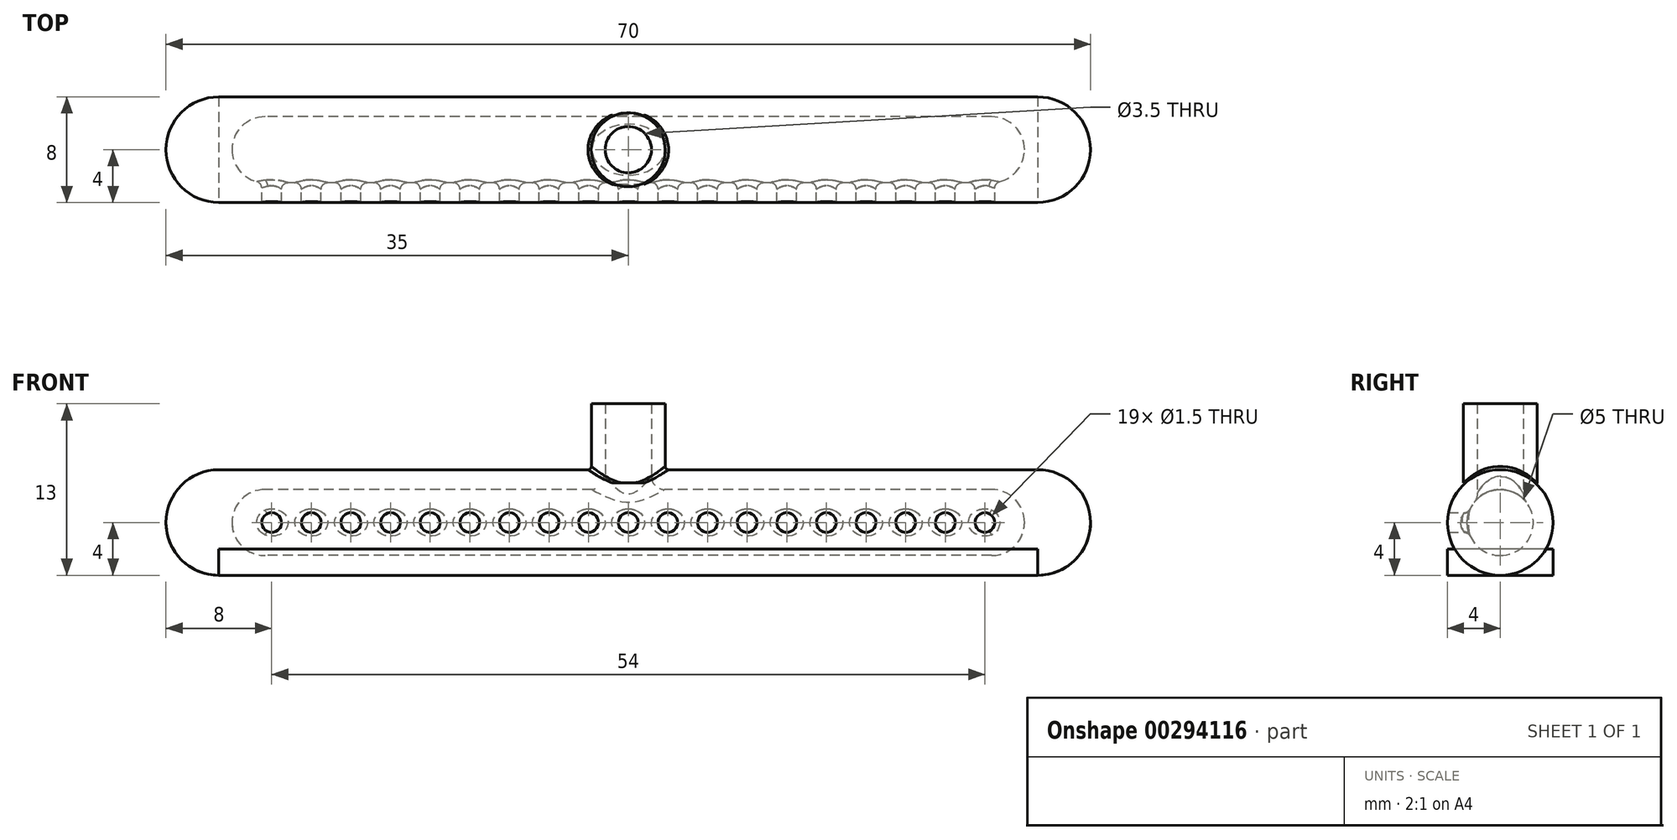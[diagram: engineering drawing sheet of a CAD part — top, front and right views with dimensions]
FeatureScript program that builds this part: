
annotation { "Feature Type Name" : "Feature", "Feature Type Description" : "" }
export const myFeature = defineFeature(function(context is Context, id is Id, definition is map)
    precondition{}
    {
        {
            var Q0;
            Q0=qCreatedBy(makeId("Top.planeOp"),FACE);
            var sketch = newSketch(context, id + "F0", { "sketchPlane" : qUnion([Q0])});
            skCircle(sketch, "E0", {"center": v(0, 0) * mm, "radius": 2.8 * mm});
            skCircle(sketch, "E1", {"center": v(0, 0) * mm, "radius": 1.75 * mm});
            skSolve(sketch);
        }
        {
            var Q0;
            Q0=makeQuery(id+"F0.imprint","IMPRINT",FACE,{"disambiguationData":[TD([[makeQuery(id+"F0.imprint","IMPRINT",EDGE,{"derivedFrom":sQuery(id+"F0.wireOp",EDGE,"E0")}),1.0]])]});
            extrude(context, id + "F1", {"entities" : qUnion([Q0]), "depth" : 6 * mm});
        }
        {
            var Q0;
            Q0=qCreatedBy(makeId("Right.planeOp"),FACE);
            var sketch = newSketch(context, id + "F2", { "sketchPlane" : qUnion([Q0])});
            skCircle(sketch, "E2", {"center": v(0, 0) * mm, "radius": 2.5 * mm});
            skSolve(sketch);
        }
        {
            var Q0;
            Q0 = qSketchRegion(id + "F2", true);
            extrude(context, id + "F3", {"entities" : qUnion([Q0]), "endBound" : BoundingType.SYMMETRIC, "depth" : 60 * mm});
        }
        {
            var Q0;
            Q0=makeQuery(id+"F3.opExtrude","SWEPT_BODY",BODY,{"disambiguationData":[OSD([sQuery(id+"F2.wireOp",EDGE,"E2")])]});
            transform(context, id + "F4", {"entities" : qUnion([Q0]), "transformType" : TransformType.TRANSLATION_3D, "dx" : 0 * mm, "dy" : 0 * mm, "dz" : -3 * mm, "makeCopy" : false});
        }
        {
            var Q0;
            Q0=makeQuery(id+"F3.opExtrude","CAP_EDGE",EDGE,{"disambiguationData":[OSD([sQuery(id+"F2.wireOp",EDGE,"E2")])],"isStart":false});
            var Q1;
            Q1=makeQuery(id+"F3.opExtrude","CAP_EDGE",EDGE,{"disambiguationData":[OSD([sQuery(id+"F2.wireOp",EDGE,"E2")])],"isStart":true});
            fillet(context, id + "F5", {"entities" : qUnion([Q0, Q1]), "radius" : 2.5 * mm, "tangentPropagation" : true, "allowEdgeOverflow" : false});
        }
        {
            var Q0;
            Q0=qCreatedBy(makeId("Top.planeOp"),FACE);
            var sketch = newSketch(context, id + "F6", { "sketchPlane" : qUnion([Q0])});
            skCircle(sketch, "E3", {"center": v(0, 0) * mm, "radius": 1.75 * mm});
            skSolve(sketch);
        }
        {
            var Q0;
            Q0 = qSketchRegion(id + "F6", true);
            extrude(context, id + "F7", {"entities" : qUnion([Q0]), "endBound" : BoundingType.SYMMETRIC, "depth" : 6 * mm});
        }
        {
            var Q0;
            Q0=makeQuery(id+"F7.opExtrude","SWEPT_BODY",BODY,{"disambiguationData":[OSD([sQuery(id+"F6.wireOp",EDGE,"E3")])]});
            var Q1;
            Q1=makeQuery(id+"F3.opExtrude","SWEPT_BODY",BODY,{"disambiguationData":[OSD([sQuery(id+"F2.wireOp",EDGE,"E2")])]});
            booleanBodies(context, id + "F8", {"operationType" : BooleanOperationType.UNION, "tools" : qUnion([Q0, Q1])});
        }
        {
            var Q0;
            Q0=qCreatedBy(makeId("Front.planeOp"),FACE);
            var sketch = newSketch(context, id + "F9", { "sketchPlane" : qUnion([Q0])});
            skCircle(sketch, "E4", {"center": v(-27, -3) * mm, "radius": 0.75 * mm});
            skCircle(sketch, "E5", {"center": v(-24, -3) * mm, "radius": 0.75 * mm});
            skCircle(sketch, "E6", {"center": v(-21, -3) * mm, "radius": 0.75 * mm});
            skCircle(sketch, "E7", {"center": v(-18, -3) * mm, "radius": 0.75 * mm});
            skCircle(sketch, "E8", {"center": v(-15, -3) * mm, "radius": 0.75 * mm});
            skCircle(sketch, "E9", {"center": v(-12, -3) * mm, "radius": 0.75 * mm});
            skCircle(sketch, "E10", {"center": v(-9, -3) * mm, "radius": 0.75 * mm});
            skCircle(sketch, "E11", {"center": v(-6, -3) * mm, "radius": 0.75 * mm});
            skCircle(sketch, "E12", {"center": v(-3, -3) * mm, "radius": 0.75 * mm});
            skCircle(sketch, "E13", {"center": v(0, -3) * mm, "radius": 0.75 * mm});
            skLineSegment(sketch, "E14.trimOffspring", {"start": v(-26.25, -3) * mm, "end": v(-27, -3) * mm});
            skLineSegment(sketch, "E15.trimOffspring", {"start": v(-23.25, -3) * mm, "end": v(-24, -3) * mm});
            skSolve(sketch);
        }
        {
            var Q0;
            Q0 = qSketchRegion(id + "F9", true);
            extrude(context, id + "F10", {"entities" : qUnion([Q0]), "depth" : 10 * mm});
        }
        {
            var Q0;
            Q0=makeQuery(id+"F10.opExtrude","SWEPT_BODY",BODY,{"disambiguationData":[OSD([sQuery(id+"F9.wireOp",EDGE,"E13")])]});
            var Q1;
            Q1=makeQuery(id+"F10.opExtrude","SWEPT_BODY",BODY,{"disambiguationData":[OSD([sQuery(id+"F9.wireOp",EDGE,"E12")])]});
            var Q2;
            Q2=makeQuery(id+"F10.opExtrude","SWEPT_BODY",BODY,{"disambiguationData":[OSD([sQuery(id+"F9.wireOp",EDGE,"E11")])]});
            var Q3;
            Q3=makeQuery(id+"F10.opExtrude","SWEPT_BODY",BODY,{"disambiguationData":[OSD([sQuery(id+"F9.wireOp",EDGE,"E10")])]});
            var Q4;
            Q4=makeQuery(id+"F10.opExtrude","SWEPT_BODY",BODY,{"disambiguationData":[OSD([sQuery(id+"F9.wireOp",EDGE,"E9")])]});
            var Q5;
            Q5=makeQuery(id+"F10.opExtrude","SWEPT_BODY",BODY,{"disambiguationData":[OSD([sQuery(id+"F9.wireOp",EDGE,"E8")])]});
            var Q6;
            Q6=makeQuery(id+"F10.opExtrude","SWEPT_BODY",BODY,{"disambiguationData":[OSD([sQuery(id+"F9.wireOp",EDGE,"E7")])]});
            var Q7;
            Q7=makeQuery(id+"F10.opExtrude","SWEPT_BODY",BODY,{"disambiguationData":[OSD([sQuery(id+"F9.wireOp",EDGE,"E6")])]});
            var Q8;
            Q8=makeQuery(id+"F10.opExtrude","SWEPT_BODY",BODY,{"disambiguationData":[OSD([sQuery(id+"F9.wireOp",EDGE,"E5")])]});
            var Q9;
            Q9=makeQuery(id+"F10.opExtrude","SWEPT_BODY",BODY,{"disambiguationData":[OSD([sQuery(id+"F9.wireOp",EDGE,"E4")])]});
            transform(context, id + "F11", {"entities" : qUnion([Q0, Q1, Q2, Q3, Q4, Q5, Q6, Q7, Q8, Q9]), "transformType" : TransformType.COPY});
        }
        {
            var Q0;
            Q0=makeQuery(id+"F11.opPattern","COPY",BODY,{"derivedFrom":makeQuery(id+"F10.opExtrude","SWEPT_BODY",BODY,{"disambiguationData":[OSD([sQuery(id+"F9.wireOp",EDGE,"E4")])]}),"instanceName":"1"});
            var Q1;
            Q1=makeQuery(id+"F11.opPattern","COPY",BODY,{"derivedFrom":makeQuery(id+"F10.opExtrude","SWEPT_BODY",BODY,{"disambiguationData":[OSD([sQuery(id+"F9.wireOp",EDGE,"E5")])]}),"instanceName":"1"});
            var Q2;
            Q2=makeQuery(id+"F11.opPattern","COPY",BODY,{"derivedFrom":makeQuery(id+"F10.opExtrude","SWEPT_BODY",BODY,{"disambiguationData":[OSD([sQuery(id+"F9.wireOp",EDGE,"E6")])]}),"instanceName":"1"});
            var Q3;
            Q3=makeQuery(id+"F11.opPattern","COPY",BODY,{"derivedFrom":makeQuery(id+"F10.opExtrude","SWEPT_BODY",BODY,{"disambiguationData":[OSD([sQuery(id+"F9.wireOp",EDGE,"E7")])]}),"instanceName":"1"});
            var Q4;
            Q4=makeQuery(id+"F11.opPattern","COPY",BODY,{"derivedFrom":makeQuery(id+"F10.opExtrude","SWEPT_BODY",BODY,{"disambiguationData":[OSD([sQuery(id+"F9.wireOp",EDGE,"E8")])]}),"instanceName":"1"});
            var Q5;
            Q5=makeQuery(id+"F11.opPattern","COPY",BODY,{"derivedFrom":makeQuery(id+"F10.opExtrude","SWEPT_BODY",BODY,{"disambiguationData":[OSD([sQuery(id+"F9.wireOp",EDGE,"E9")])]}),"instanceName":"1"});
            var Q6;
            Q6=makeQuery(id+"F11.opPattern","COPY",BODY,{"derivedFrom":makeQuery(id+"F10.opExtrude","SWEPT_BODY",BODY,{"disambiguationData":[OSD([sQuery(id+"F9.wireOp",EDGE,"E10")])]}),"instanceName":"1"});
            var Q7;
            Q7=makeQuery(id+"F11.opPattern","COPY",BODY,{"derivedFrom":makeQuery(id+"F10.opExtrude","SWEPT_BODY",BODY,{"disambiguationData":[OSD([sQuery(id+"F9.wireOp",EDGE,"E11")])]}),"instanceName":"1"});
            var Q8;
            Q8=makeQuery(id+"F11.opPattern","COPY",BODY,{"derivedFrom":makeQuery(id+"F10.opExtrude","SWEPT_BODY",BODY,{"disambiguationData":[OSD([sQuery(id+"F9.wireOp",EDGE,"E12")])]}),"instanceName":"1"});
            var Q9;
            Q9=makeQuery(id+"F11.opPattern","COPY",BODY,{"derivedFrom":makeQuery(id+"F10.opExtrude","SWEPT_BODY",BODY,{"disambiguationData":[OSD([sQuery(id+"F9.wireOp",EDGE,"E13")])]}),"instanceName":"1"});
            transform(context, id + "F12", {"entities" : qUnion([Q0, Q1, Q2, Q3, Q4, Q5, Q6, Q7, Q8, Q9]), "transformType" : TransformType.TRANSLATION_3D, "dx" : 27 * mm, "dy" : 0 * mm, "dz" : 0 * mm, "makeCopy" : false});
        }
        {
            var Q0;
            Q0=makeQuery(id+"F11.opPattern","COPY",BODY,{"derivedFrom":makeQuery(id+"F10.opExtrude","SWEPT_BODY",BODY,{"disambiguationData":[OSD([sQuery(id+"F9.wireOp",EDGE,"E13")])]}),"instanceName":"1"});
            var Q1;
            Q1=makeQuery(id+"F11.opPattern","COPY",BODY,{"derivedFrom":makeQuery(id+"F10.opExtrude","SWEPT_BODY",BODY,{"disambiguationData":[OSD([sQuery(id+"F9.wireOp",EDGE,"E12")])]}),"instanceName":"1"});
            var Q2;
            Q2=makeQuery(id+"F11.opPattern","COPY",BODY,{"derivedFrom":makeQuery(id+"F10.opExtrude","SWEPT_BODY",BODY,{"disambiguationData":[OSD([sQuery(id+"F9.wireOp",EDGE,"E11")])]}),"instanceName":"1"});
            var Q3;
            Q3=makeQuery(id+"F11.opPattern","COPY",BODY,{"derivedFrom":makeQuery(id+"F10.opExtrude","SWEPT_BODY",BODY,{"disambiguationData":[OSD([sQuery(id+"F9.wireOp",EDGE,"E10")])]}),"instanceName":"1"});
            var Q4;
            Q4=makeQuery(id+"F11.opPattern","COPY",BODY,{"derivedFrom":makeQuery(id+"F10.opExtrude","SWEPT_BODY",BODY,{"disambiguationData":[OSD([sQuery(id+"F9.wireOp",EDGE,"E9")])]}),"instanceName":"1"});
            var Q5;
            Q5=makeQuery(id+"F11.opPattern","COPY",BODY,{"derivedFrom":makeQuery(id+"F10.opExtrude","SWEPT_BODY",BODY,{"disambiguationData":[OSD([sQuery(id+"F9.wireOp",EDGE,"E8")])]}),"instanceName":"1"});
            var Q6;
            Q6=makeQuery(id+"F11.opPattern","COPY",BODY,{"derivedFrom":makeQuery(id+"F10.opExtrude","SWEPT_BODY",BODY,{"disambiguationData":[OSD([sQuery(id+"F9.wireOp",EDGE,"E7")])]}),"instanceName":"1"});
            var Q7;
            Q7=makeQuery(id+"F11.opPattern","COPY",BODY,{"derivedFrom":makeQuery(id+"F10.opExtrude","SWEPT_BODY",BODY,{"disambiguationData":[OSD([sQuery(id+"F9.wireOp",EDGE,"E6")])]}),"instanceName":"1"});
            var Q8;
            Q8=makeQuery(id+"F11.opPattern","COPY",BODY,{"derivedFrom":makeQuery(id+"F10.opExtrude","SWEPT_BODY",BODY,{"disambiguationData":[OSD([sQuery(id+"F9.wireOp",EDGE,"E5")])]}),"instanceName":"1"});
            var Q9;
            Q9=makeQuery(id+"F11.opPattern","COPY",BODY,{"derivedFrom":makeQuery(id+"F10.opExtrude","SWEPT_BODY",BODY,{"disambiguationData":[OSD([sQuery(id+"F9.wireOp",EDGE,"E4")])]}),"instanceName":"1"});
            var Q10;
            Q10=makeQuery(id+"F10.opExtrude","SWEPT_BODY",BODY,{"disambiguationData":[OSD([sQuery(id+"F9.wireOp",EDGE,"E13")])]});
            var Q11;
            Q11=makeQuery(id+"F10.opExtrude","SWEPT_BODY",BODY,{"disambiguationData":[OSD([sQuery(id+"F9.wireOp",EDGE,"E12")])]});
            var Q12;
            Q12=makeQuery(id+"F10.opExtrude","SWEPT_BODY",BODY,{"disambiguationData":[OSD([sQuery(id+"F9.wireOp",EDGE,"E11")])]});
            var Q13;
            Q13=makeQuery(id+"F10.opExtrude","SWEPT_BODY",BODY,{"disambiguationData":[OSD([sQuery(id+"F9.wireOp",EDGE,"E10")])]});
            var Q14;
            Q14=makeQuery(id+"F10.opExtrude","SWEPT_BODY",BODY,{"disambiguationData":[OSD([sQuery(id+"F9.wireOp",EDGE,"E9")])]});
            var Q15;
            Q15=makeQuery(id+"F10.opExtrude","SWEPT_BODY",BODY,{"disambiguationData":[OSD([sQuery(id+"F9.wireOp",EDGE,"E8")])]});
            var Q16;
            Q16=makeQuery(id+"F10.opExtrude","SWEPT_BODY",BODY,{"disambiguationData":[OSD([sQuery(id+"F9.wireOp",EDGE,"E7")])]});
            var Q17;
            Q17=makeQuery(id+"F10.opExtrude","SWEPT_BODY",BODY,{"disambiguationData":[OSD([sQuery(id+"F9.wireOp",EDGE,"E6")])]});
            var Q18;
            Q18=makeQuery(id+"F10.opExtrude","SWEPT_BODY",BODY,{"disambiguationData":[OSD([sQuery(id+"F9.wireOp",EDGE,"E5")])]});
            var Q19;
            Q19=makeQuery(id+"F10.opExtrude","SWEPT_BODY",BODY,{"disambiguationData":[OSD([sQuery(id+"F9.wireOp",EDGE,"E4")])]});
            var Q20;
            Q20=makeQuery(id+"F7.opExtrude","SWEPT_BODY",BODY,{"disambiguationData":[OSD([sQuery(id+"F6.wireOp",EDGE,"E3")])]});
            booleanBodies(context, id + "F13", {"operationType" : BooleanOperationType.UNION, "tools" : qUnion([Q0, Q1, Q2, Q3, Q4, Q5, Q6, Q7, Q8, Q9, Q10, Q11, Q12, Q13, Q14, Q15, Q16, Q17, Q18, Q19, Q20])});
        }
        {
            var Q0;
            Q0=makeQuery(id+"F13.opBoolean","INTERSECT",EDGE,{"derivedFrom":[makeQuery(id+"F3.opExtrude","SWEPT_FACE",FACE,{"disambiguationData":[OSD([sQuery(id+"F2.wireOp",EDGE,"E2")])]}),makeQuery(id+"F10.opExtrude","SWEPT_FACE",FACE,{"disambiguationData":[OSD([sQuery(id+"F9.wireOp",EDGE,"E4")])]})]});
            var Q1;
            Q1=makeQuery(id+"F13.opBoolean","INTERSECT",EDGE,{"derivedFrom":[makeQuery(id+"F3.opExtrude","SWEPT_FACE",FACE,{"disambiguationData":[OSD([sQuery(id+"F2.wireOp",EDGE,"E2")])]}),makeQuery(id+"F10.opExtrude","SWEPT_FACE",FACE,{"disambiguationData":[OSD([sQuery(id+"F9.wireOp",EDGE,"E5")])]})]});
            var Q2;
            Q2=makeQuery(id+"F13.opBoolean","INTERSECT",EDGE,{"derivedFrom":[makeQuery(id+"F3.opExtrude","SWEPT_FACE",FACE,{"disambiguationData":[OSD([sQuery(id+"F2.wireOp",EDGE,"E2")])]}),makeQuery(id+"F10.opExtrude","SWEPT_FACE",FACE,{"disambiguationData":[OSD([sQuery(id+"F9.wireOp",EDGE,"E6")])]})]});
            var Q3;
            Q3=makeQuery(id+"F13.opBoolean","INTERSECT",EDGE,{"derivedFrom":[makeQuery(id+"F3.opExtrude","SWEPT_FACE",FACE,{"disambiguationData":[OSD([sQuery(id+"F2.wireOp",EDGE,"E2")])]}),makeQuery(id+"F10.opExtrude","SWEPT_FACE",FACE,{"disambiguationData":[OSD([sQuery(id+"F9.wireOp",EDGE,"E7")])]})]});
            var Q4;
            Q4=makeQuery(id+"F13.opBoolean","INTERSECT",EDGE,{"derivedFrom":[makeQuery(id+"F3.opExtrude","SWEPT_FACE",FACE,{"disambiguationData":[OSD([sQuery(id+"F2.wireOp",EDGE,"E2")])]}),makeQuery(id+"F10.opExtrude","SWEPT_FACE",FACE,{"disambiguationData":[OSD([sQuery(id+"F9.wireOp",EDGE,"E8")])]})]});
            var Q5;
            Q5=makeQuery(id+"F13.opBoolean","INTERSECT",EDGE,{"derivedFrom":[makeQuery(id+"F3.opExtrude","SWEPT_FACE",FACE,{"disambiguationData":[OSD([sQuery(id+"F2.wireOp",EDGE,"E2")])]}),makeQuery(id+"F10.opExtrude","SWEPT_FACE",FACE,{"disambiguationData":[OSD([sQuery(id+"F9.wireOp",EDGE,"E9")])]})]});
            var Q6;
            Q6=makeQuery(id+"F13.opBoolean","INTERSECT",EDGE,{"derivedFrom":[makeQuery(id+"F3.opExtrude","SWEPT_FACE",FACE,{"disambiguationData":[OSD([sQuery(id+"F2.wireOp",EDGE,"E2")])]}),makeQuery(id+"F10.opExtrude","SWEPT_FACE",FACE,{"disambiguationData":[OSD([sQuery(id+"F9.wireOp",EDGE,"E10")])]})]});
            var Q7;
            Q7=makeQuery(id+"F13.opBoolean","INTERSECT",EDGE,{"derivedFrom":[makeQuery(id+"F3.opExtrude","SWEPT_FACE",FACE,{"disambiguationData":[OSD([sQuery(id+"F2.wireOp",EDGE,"E2")])]}),makeQuery(id+"F10.opExtrude","SWEPT_FACE",FACE,{"disambiguationData":[OSD([sQuery(id+"F9.wireOp",EDGE,"E11")])]})]});
            var Q8;
            Q8=makeQuery(id+"F13.opBoolean","INTERSECT",EDGE,{"derivedFrom":[makeQuery(id+"F3.opExtrude","SWEPT_FACE",FACE,{"disambiguationData":[OSD([sQuery(id+"F2.wireOp",EDGE,"E2")])]}),makeQuery(id+"F10.opExtrude","SWEPT_FACE",FACE,{"disambiguationData":[OSD([sQuery(id+"F9.wireOp",EDGE,"E12")])]})]});
            var Q9;
            Q9=makeQuery(id+"F13.opBoolean","INTERSECT",EDGE,{"derivedFrom":[makeQuery(id+"F3.opExtrude","SWEPT_FACE",FACE,{"disambiguationData":[OSD([sQuery(id+"F2.wireOp",EDGE,"E2")])]}),makeQuery(id+"F10.opExtrude","SWEPT_FACE",FACE,{"disambiguationData":[OSD([sQuery(id+"F9.wireOp",EDGE,"E13")])]}),makeQuery(id+"F11.opPattern","COPY",FACE,{"derivedFrom":makeQuery(id+"F10.opExtrude","SWEPT_FACE",FACE,{"disambiguationData":[OSD([sQuery(id+"F9.wireOp",EDGE,"E4")])]}),"instanceName":"1"})]});
            var Q10;
            Q10=makeQuery(id+"F13.opBoolean","INTERSECT",EDGE,{"derivedFrom":[makeQuery(id+"F3.opExtrude","SWEPT_FACE",FACE,{"disambiguationData":[OSD([sQuery(id+"F2.wireOp",EDGE,"E2")])]}),makeQuery(id+"F11.opPattern","COPY",FACE,{"derivedFrom":makeQuery(id+"F10.opExtrude","SWEPT_FACE",FACE,{"disambiguationData":[OSD([sQuery(id+"F9.wireOp",EDGE,"E5")])]}),"instanceName":"1"})]});
            var Q11;
            Q11=makeQuery(id+"F13.opBoolean","INTERSECT",EDGE,{"derivedFrom":[makeQuery(id+"F3.opExtrude","SWEPT_FACE",FACE,{"disambiguationData":[OSD([sQuery(id+"F2.wireOp",EDGE,"E2")])]}),makeQuery(id+"F11.opPattern","COPY",FACE,{"derivedFrom":makeQuery(id+"F10.opExtrude","SWEPT_FACE",FACE,{"disambiguationData":[OSD([sQuery(id+"F9.wireOp",EDGE,"E6")])]}),"instanceName":"1"})]});
            var Q12;
            Q12=makeQuery(id+"F13.opBoolean","INTERSECT",EDGE,{"derivedFrom":[makeQuery(id+"F3.opExtrude","SWEPT_FACE",FACE,{"disambiguationData":[OSD([sQuery(id+"F2.wireOp",EDGE,"E2")])]}),makeQuery(id+"F11.opPattern","COPY",FACE,{"derivedFrom":makeQuery(id+"F10.opExtrude","SWEPT_FACE",FACE,{"disambiguationData":[OSD([sQuery(id+"F9.wireOp",EDGE,"E7")])]}),"instanceName":"1"})]});
            var Q13;
            Q13=makeQuery(id+"F13.opBoolean","INTERSECT",EDGE,{"derivedFrom":[makeQuery(id+"F3.opExtrude","SWEPT_FACE",FACE,{"disambiguationData":[OSD([sQuery(id+"F2.wireOp",EDGE,"E2")])]}),makeQuery(id+"F11.opPattern","COPY",FACE,{"derivedFrom":makeQuery(id+"F10.opExtrude","SWEPT_FACE",FACE,{"disambiguationData":[OSD([sQuery(id+"F9.wireOp",EDGE,"E8")])]}),"instanceName":"1"})]});
            var Q14;
            Q14=makeQuery(id+"F13.opBoolean","INTERSECT",EDGE,{"derivedFrom":[makeQuery(id+"F3.opExtrude","SWEPT_FACE",FACE,{"disambiguationData":[OSD([sQuery(id+"F2.wireOp",EDGE,"E2")])]}),makeQuery(id+"F11.opPattern","COPY",FACE,{"derivedFrom":makeQuery(id+"F10.opExtrude","SWEPT_FACE",FACE,{"disambiguationData":[OSD([sQuery(id+"F9.wireOp",EDGE,"E9")])]}),"instanceName":"1"})]});
            var Q15;
            Q15=makeQuery(id+"F13.opBoolean","INTERSECT",EDGE,{"derivedFrom":[makeQuery(id+"F3.opExtrude","SWEPT_FACE",FACE,{"disambiguationData":[OSD([sQuery(id+"F2.wireOp",EDGE,"E2")])]}),makeQuery(id+"F11.opPattern","COPY",FACE,{"derivedFrom":makeQuery(id+"F10.opExtrude","SWEPT_FACE",FACE,{"disambiguationData":[OSD([sQuery(id+"F9.wireOp",EDGE,"E10")])]}),"instanceName":"1"})]});
            var Q16;
            Q16=makeQuery(id+"F13.opBoolean","INTERSECT",EDGE,{"derivedFrom":[makeQuery(id+"F3.opExtrude","SWEPT_FACE",FACE,{"disambiguationData":[OSD([sQuery(id+"F2.wireOp",EDGE,"E2")])]}),makeQuery(id+"F11.opPattern","COPY",FACE,{"derivedFrom":makeQuery(id+"F10.opExtrude","SWEPT_FACE",FACE,{"disambiguationData":[OSD([sQuery(id+"F9.wireOp",EDGE,"E11")])]}),"instanceName":"1"})]});
            var Q17;
            Q17=makeQuery(id+"F13.opBoolean","INTERSECT",EDGE,{"derivedFrom":[makeQuery(id+"F3.opExtrude","SWEPT_FACE",FACE,{"disambiguationData":[OSD([sQuery(id+"F2.wireOp",EDGE,"E2")])]}),makeQuery(id+"F11.opPattern","COPY",FACE,{"derivedFrom":makeQuery(id+"F10.opExtrude","SWEPT_FACE",FACE,{"disambiguationData":[OSD([sQuery(id+"F9.wireOp",EDGE,"E12")])]}),"instanceName":"1"})]});
            var Q18;
            Q18=makeQuery(id+"F13.opBoolean","INTERSECT",EDGE,{"derivedFrom":[makeQuery(id+"F3.opExtrude","SWEPT_FACE",FACE,{"disambiguationData":[OSD([sQuery(id+"F2.wireOp",EDGE,"E2")])]}),makeQuery(id+"F11.opPattern","COPY",FACE,{"derivedFrom":makeQuery(id+"F10.opExtrude","SWEPT_FACE",FACE,{"disambiguationData":[OSD([sQuery(id+"F9.wireOp",EDGE,"E13")])]}),"instanceName":"1"})]});
            fillet(context, id + "F14", {"entities" : qUnion([Q0, Q1, Q2, Q3, Q4, Q5, Q6, Q7, Q8, Q9, Q10, Q11, Q12, Q13, Q14, Q15, Q16, Q17, Q18]), "radius" : 0.5 * mm, "tangentPropagation" : true, "allowEdgeOverflow" : false});
        }
        {
            var Q0;
            Q0=makeQuery(id+"F8.opBoolean","INTERSECT",EDGE,{"derivedFrom":[makeQuery(id+"F3.opExtrude","SWEPT_FACE",FACE,{"disambiguationData":[OSD([sQuery(id+"F2.wireOp",EDGE,"E2")])]}),makeQuery(id+"F7.opExtrude","SWEPT_FACE",FACE,{"disambiguationData":[OSD([sQuery(id+"F6.wireOp",EDGE,"E3")])]})]});
            fillet(context, id + "F15", {"entities" : qUnion([Q0]), "radius" : 1 * mm, "tangentPropagation" : true, "allowEdgeOverflow" : false});
        }
        {
            var Q0;
            Q0=qCreatedBy(makeId("Right.planeOp"),FACE);
            var sketch = newSketch(context, id + "F16", { "sketchPlane" : qUnion([Q0])});
            skLineSegment(sketch, "E16", {"start": v(0, 0) * mm, "end": v(0, -3) * mm});
            skCircle(sketch, "E17", {"center": v(0, -3) * mm, "radius": 4 * mm});
            skSolve(sketch);
        }
        {
            var Q0;
            Q0 = qSketchRegion(id + "F16", true);
            extrude(context, id + "F17", {"entities" : qUnion([Q0]), "endBound" : BoundingType.SYMMETRIC, "depth" : 70 * mm});
        }
        {
            var Q0;
            Q0=makeQuery(id+"F17.opExtrude","CAP_EDGE",EDGE,{"disambiguationData":[OSD([sQuery(id+"F16.wireOp",EDGE,"E17")])],"isStart":false});
            var Q1;
            Q1=makeQuery(id+"F17.opExtrude","CAP_EDGE",EDGE,{"disambiguationData":[OSD([sQuery(id+"F16.wireOp",EDGE,"E17")])],"isStart":true});
            fillet(context, id + "F18", {"entities" : qUnion([Q0, Q1]), "radius" : 4 * mm, "tangentPropagation" : true, "allowEdgeOverflow" : false});
        }
        {
            var Q0;
            Q0=makeQuery(id+"F1.opExtrude","SWEPT_BODY",BODY,{"disambiguationData":[OSD([sQuery(id+"F0.wireOp",EDGE,"E0"),sQuery(id+"F0.wireOp",EDGE,"E1")])]});
            var Q1;
            Q1=makeQuery(id+"F17.opExtrude","SWEPT_BODY",BODY,{"disambiguationData":[OSD([sQuery(id+"F16.wireOp",EDGE,"E17")])]});
            booleanBodies(context, id + "F19", {"operationType" : BooleanOperationType.UNION, "tools" : qUnion([Q0, Q1])});
        }
        {
            var Q0;
            Q0=makeQuery(id+"F19.opBoolean","INTERSECT",EDGE,{"disambiguationData":[OD(1.0)],"derivedFrom":[makeQuery(id+"F1.opExtrude","SWEPT_FACE",FACE,{"disambiguationData":[OSD([sQuery(id+"F0.wireOp",EDGE,"E0")])]}),makeQuery(id+"F17.opExtrude","SWEPT_FACE",FACE,{"disambiguationData":[OSD([sQuery(id+"F16.wireOp",EDGE,"E17")])]})]});
            var Q1;
            Q1=makeQuery(id+"F19.opBoolean","INTERSECT",EDGE,{"disambiguationData":[OD(0.0)],"derivedFrom":[makeQuery(id+"F1.opExtrude","SWEPT_FACE",FACE,{"disambiguationData":[OSD([sQuery(id+"F0.wireOp",EDGE,"E0")])]}),makeQuery(id+"F17.opExtrude","SWEPT_FACE",FACE,{"disambiguationData":[OSD([sQuery(id+"F16.wireOp",EDGE,"E17")])]})]});
            fillet(context, id + "F20", {"entities" : qUnion([Q0, Q1]), "radius" : 0.25 * mm, "tangentPropagation" : true, "allowEdgeOverflow" : false});
        }
        {
            var Q0;
            Q0=makeQuery(id+"F11.opPattern","COPY",BODY,{"derivedFrom":makeQuery(id+"F10.opExtrude","SWEPT_BODY",BODY,{"disambiguationData":[OSD([sQuery(id+"F9.wireOp",EDGE,"E13")])]}),"instanceName":"1"});
            var Q1;
            Q1=makeQuery(id+"F1.opExtrude","SWEPT_BODY",BODY,{"disambiguationData":[OSD([sQuery(id+"F0.wireOp",EDGE,"E0"),sQuery(id+"F0.wireOp",EDGE,"E1")])]});
            booleanBodies(context, id + "F21", {"operationType" : BooleanOperationType.SUBTRACTION, "tools" : qUnion([Q0]), "targets" : qUnion([Q1])});
        }
        {
            var Q0;
            Q0=qCreatedBy(makeId("Right.planeOp"),FACE);
            var sketch = newSketch(context, id + "F22", { "sketchPlane" : qUnion([Q0])});
            skLineSegment(sketch, "E18", {"start": v(0, 0) * mm, "end": v(0, -7) * mm});
            skLineSegment(sketch, "E19", {"start": v(0, -7) * mm, "end": v(-4, -7) * mm});
            skLineSegment(sketch, "E20", {"start": v(0, -7) * mm, "end": v(4, -7) * mm});
            skLineSegment(sketch, "E21", {"start": v(4, -7) * mm, "end": v(4, -5) * mm});
            skLineSegment(sketch, "E22", {"start": v(4, -5) * mm, "end": v(-4, -5) * mm});
            skLineSegment(sketch, "E23", {"start": v(-4, -5) * mm, "end": v(-4, -7) * mm});
            skSolve(sketch);
        }
        {
            var Q0;
            Q0 = qSketchRegion(id + "F22", true);
            extrude(context, id + "F23", {"entities" : qUnion([Q0]), "endBound" : BoundingType.SYMMETRIC, "depth" : 62 * mm});
        }
    });
